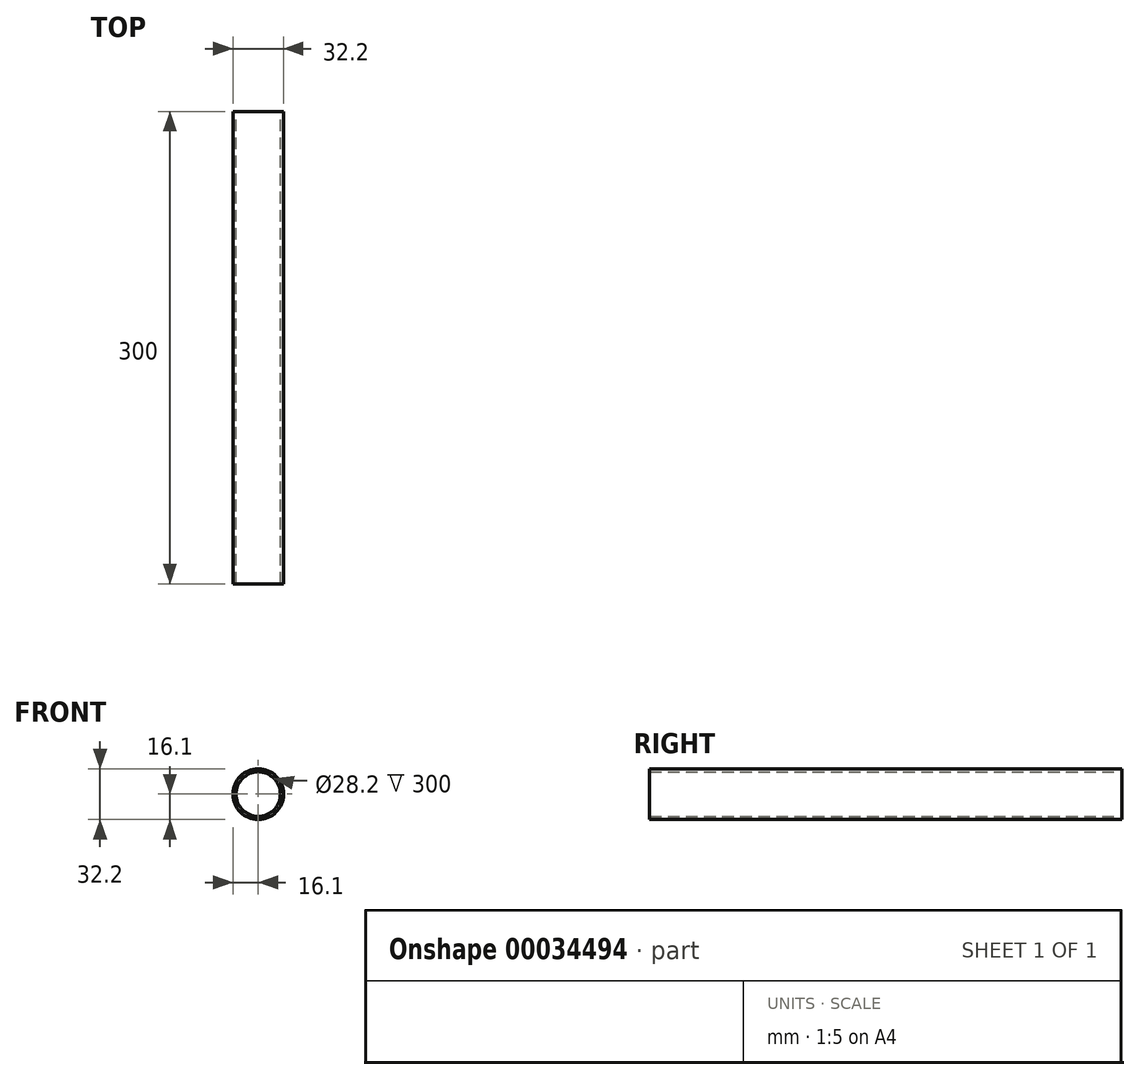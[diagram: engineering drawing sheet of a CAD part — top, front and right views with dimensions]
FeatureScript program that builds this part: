
annotation { "Feature Type Name" : "Feature", "Feature Type Description" : "" }
export const myFeature = defineFeature(function(context is Context, id is Id, definition is map)
    precondition{}
    {
        {
            var Q0;
            Q0=qCreatedBy(makeId("Front.planeOp"),FACE);
            var sketch = newSketch(context, id + "F0", { "sketchPlane" : qUnion([Q0])});
            skCircle(sketch, "E0", {"center": v(0, 0) * mm, "radius": 16.1 * mm});
            skCircle(sketch, "E1.0", {"center": v(0, 0) * mm, "radius": 14.1 * mm});
            skSolve(sketch);
        }
        {
            var Q0;
            Q0 = qSketchRegion(id + "F0", true);
            extrude(context, id + "F1", {"entities" : qUnion([Q0]), "depth" : 300 * mm});
        }
    });
